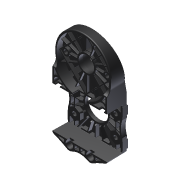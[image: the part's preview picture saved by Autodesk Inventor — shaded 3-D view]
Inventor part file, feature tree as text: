
AUTODESK INVENTOR PART (.ipt)
format: ipt  version: 2015 (Build 190159000, 159)  size: 7,671,808 bytes
history: native  units: in
note: dims shown in document units (in); Inventor stores cm internally (conversion verified against a paired STEP export)
features: chamfer x1, other x1, imported_body x1
ambient origin geometry x8: Origin, YZ Plane, XZ Plane, XY Plane, X Axis, Y Axis, Z Axis, Center Point
bodies: Body1 (feature_tree)
feature tree (3):
  chamfer  "Chamfer2"  [1 undecoded]
  other  "217-4156-001 Rev6.ipt1"
  imported_body  "Base1"
note: 1 required parameter value undecoded (feature->parameter linkage not recoverable at this tier; creation-order binding heuristic only, values carry confidence <= 0.55)
